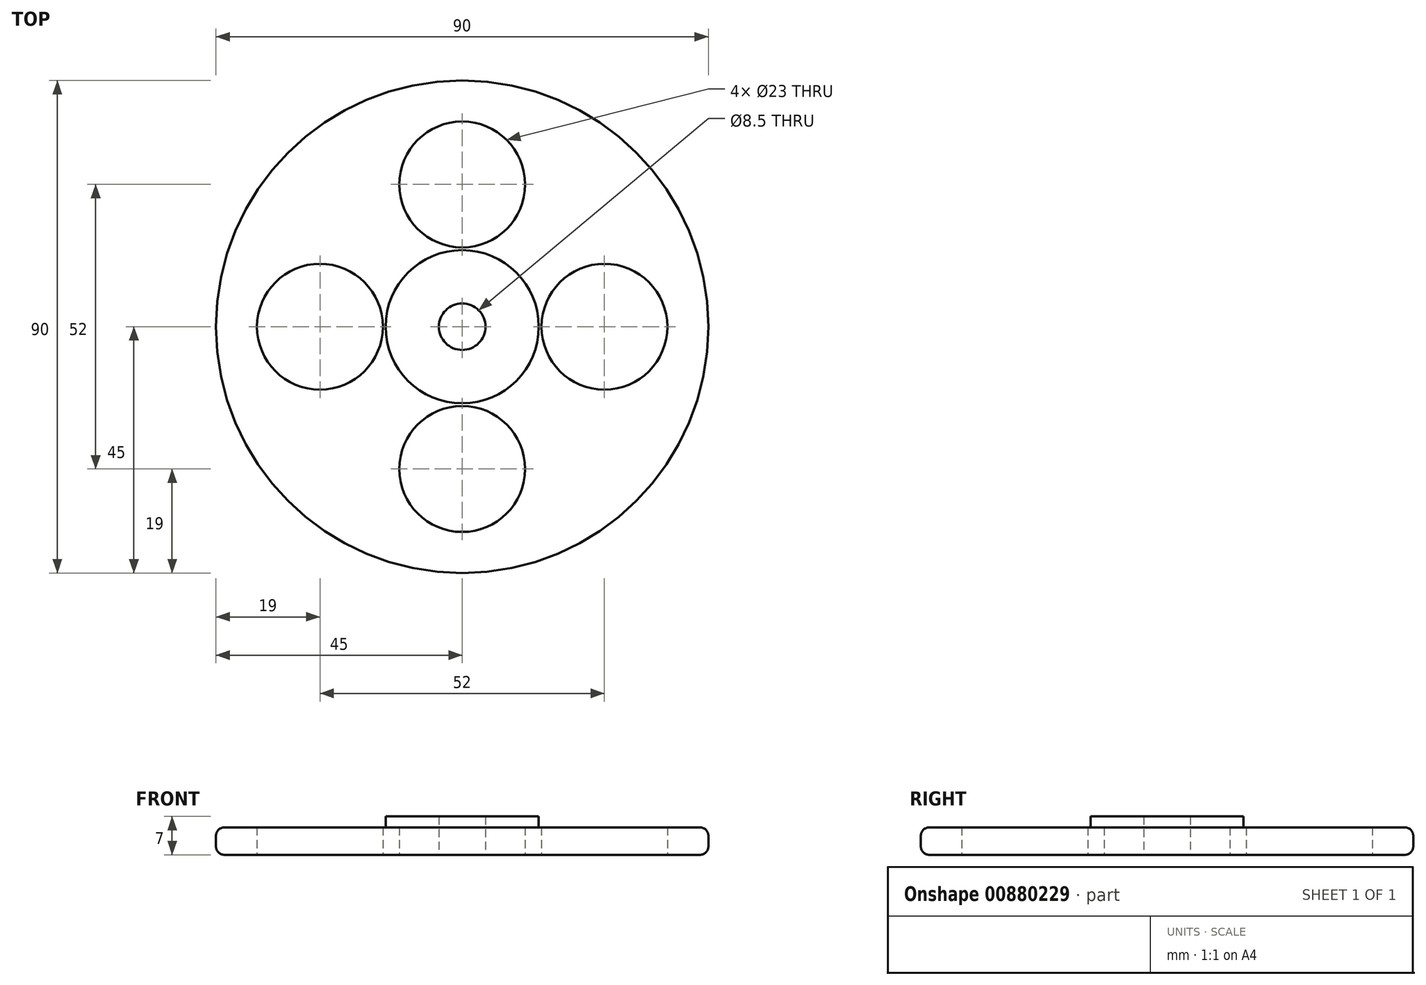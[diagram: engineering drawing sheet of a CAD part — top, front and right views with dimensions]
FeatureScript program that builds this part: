
annotation { "Feature Type Name" : "Feature", "Feature Type Description" : "" }
export const myFeature = defineFeature(function(context is Context, id is Id, definition is map)
    precondition{}
    {
        {
            var Q0;
            Q0=qCreatedBy(makeId("Top.planeOp"),FACE);
            var sketch = newSketch(context, id + "F0", { "sketchPlane" : qUnion([Q0])});
            skCircle(sketch, "E0", {"center": v(0, 0) * mm, "radius": 45 * mm});
            skCircle(sketch, "E1", {"center": v(0, 0) * mm, "radius": 4.25 * mm});
            skCircle(sketch, "E2", {"center": v(0, 0) * mm, "radius": 37.5 * mm});
            skCircle(sketch, "E3", {"center": v(0, 0) * mm, "radius": 14 * mm});
            skCircle(sketch, "E4", {"center": v(0, 0) * mm, "radius": 26 * mm});
            skCircle(sketch, "E5", {"center": v(26, 0) * mm, "radius": 11.5 * mm});
            skCircle(sketch, "E6", {"center": v(0, 26) * mm, "radius": 11.5 * mm});
            skCircle(sketch, "E7", {"center": v(-26, 0) * mm, "radius": 11.5 * mm});
            skCircle(sketch, "E8", {"center": v(0, -26) * mm, "radius": 11.5 * mm});
            skSolve(sketch);
        }
        {
            var Q0;
            {var subQ0=sQuery(id+"F0.wireOp",EDGE,"E6");var subQ1=sQuery(id+"F0.wireOp",EDGE,"E2");var subQ2=makeQuery(id+"F0.imprint","INTERSECT",VERTEX,{"derivedFrom":[subQ1,subQ0]});Q0=makeQuery(id+"F0.imprint","IMPRINT",FACE,{"disambiguationData":[TD([[makeQuery(id+"F0.imprint","IMPRINT",EDGE,{"disambiguationData":[TD([[subQ2,-1.0]])],"derivedFrom":subQ1}),1.0]])]});}
            var Q1;
            {var subQ0=sQuery(id+"F0.wireOp",EDGE,"E6");var subQ1=sQuery(id+"F0.wireOp",EDGE,"E2");var subQ2=makeQuery(id+"F0.imprint","INTERSECT",VERTEX,{"derivedFrom":[subQ1,subQ0]});Q1=makeQuery(id+"F0.imprint","IMPRINT",FACE,{"disambiguationData":[TD([[makeQuery(id+"F0.imprint","IMPRINT",EDGE,{"disambiguationData":[TD([[subQ2,1.0]])],"derivedFrom":subQ1}),1.0]])]});}
            var Q2;
            Q2=makeQuery(id+"F0.imprint","IMPRINT",FACE,{"disambiguationData":[TD([[makeQuery(id+"F0.imprint","IMPRINT",EDGE,{"derivedFrom":sQuery(id+"F0.wireOp",EDGE,"E3")}),-1.0]])]});
            var Q3;
            {var subQ0=sQuery(id+"F0.wireOp",EDGE,"E7");var subQ1=sQuery(id+"F0.wireOp",EDGE,"E2");var subQ2=makeQuery(id+"F0.imprint","INTERSECT",VERTEX,{"derivedFrom":[subQ1,subQ0]});Q3=makeQuery(id+"F0.imprint","IMPRINT",FACE,{"disambiguationData":[TD([[makeQuery(id+"F0.imprint","IMPRINT",EDGE,{"disambiguationData":[TD([[subQ2,-1.0]])],"derivedFrom":subQ1}),1.0]])]});}
            var Q4;
            {var subQ0=sQuery(id+"F0.wireOp",EDGE,"E5");var subQ1=sQuery(id+"F0.wireOp",EDGE,"E2");var subQ2=makeQuery(id+"F0.imprint","INTERSECT",VERTEX,{"derivedFrom":[subQ1,subQ0]});Q4=makeQuery(id+"F0.imprint","IMPRINT",FACE,{"disambiguationData":[TD([[makeQuery(id+"F0.imprint","IMPRINT",EDGE,{"disambiguationData":[TD([[subQ2,1.0]])],"derivedFrom":subQ1}),1.0]])]});}
            var Q5;
            Q5=makeQuery(id+"F0.imprint","IMPRINT",FACE,{"disambiguationData":[TD([[makeQuery(id+"F0.imprint","IMPRINT",EDGE,{"derivedFrom":sQuery(id+"F0.wireOp",EDGE,"E0")}),1.0]])]});
            extrude(context, id + "F1", {"entities" : qUnion([Q0, Q1, Q2, Q3, Q4, Q5]), "depth" : 5 * mm, "offsetDistance" : 25 * mm});
        }
        {
            var Q0;
            Q0=makeQuery(id+"F0.imprint","IMPRINT",FACE,{"disambiguationData":[TD([[makeQuery(id+"F0.imprint","IMPRINT",EDGE,{"derivedFrom":sQuery(id+"F0.wireOp",EDGE,"E1")}),-1.0]])]});
            extrude(context, id + "F2", {"entities" : qUnion([Q0]), "operationType" : NewBodyOperationType.ADD, "depth" : 7 * mm, "offsetDistance" : 25 * mm});
        }
        {
            var Q0;
            Q0=makeQuery(id+"F1.opExtrude","CAP_EDGE",EDGE,{"disambiguationData":[OSD([sQuery(id+"F0.wireOp",EDGE,"E0")])],"isStart":false});
            var Q1;
            Q1=makeQuery(id+"F1.opExtrude","CAP_EDGE",EDGE,{"disambiguationData":[OSD([sQuery(id+"F0.wireOp",EDGE,"E0")])],"isStart":true});
            fillet(context, id + "F3", {"entities" : qUnion([Q0, Q1]), "radius" : 1.5 * mm, "tangentPropagation" : true, "allowEdgeOverflow" : false});
        }
    });
